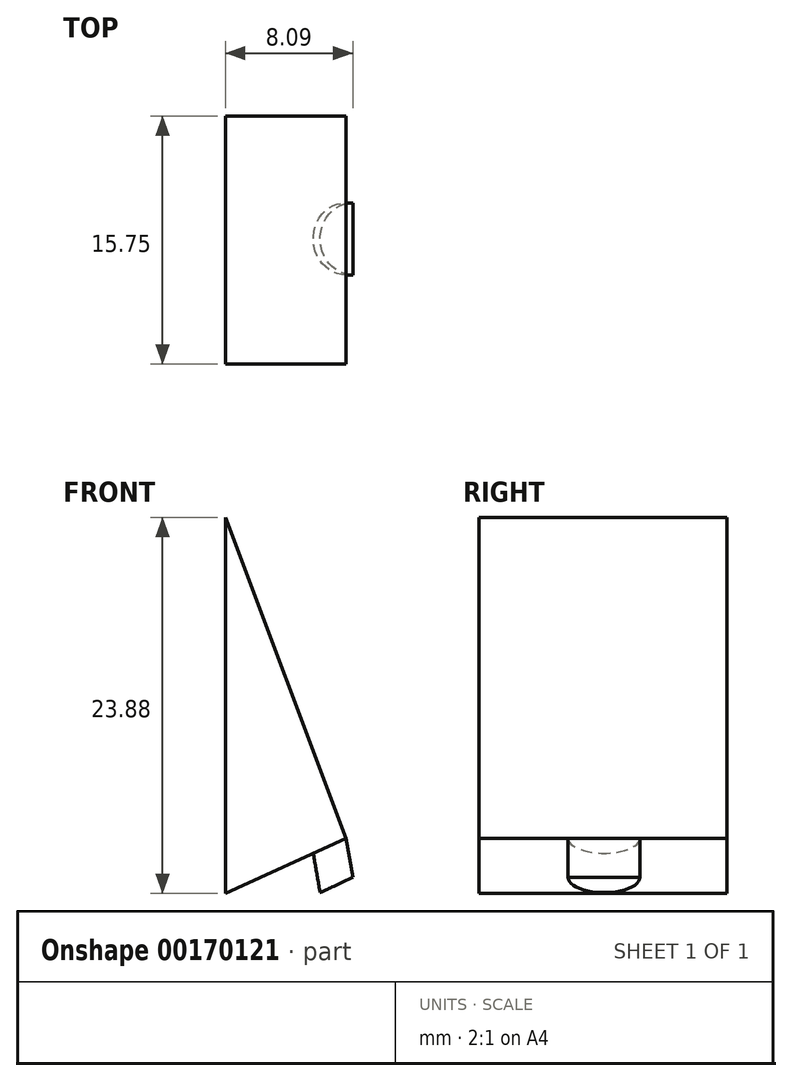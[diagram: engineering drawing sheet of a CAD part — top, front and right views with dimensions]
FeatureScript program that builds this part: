
annotation { "Feature Type Name" : "Feature", "Feature Type Description" : "" }
export const myFeature = defineFeature(function(context is Context, id is Id, definition is map)
    precondition{}
    {
        {
            var Q0;
            Q0=qCreatedBy(makeId("Front.planeOp"),FACE);
            var sketch = newSketch(context, id + "F0", { "sketchPlane" : qUnion([Q0])});
            skLineSegment(sketch, "E0", {"start": v(0, 0) * mm, "end": v(0, 23.88) * mm});
            skLineSegment(sketch, "E1", {"start": v(0, 23.88) * mm, "end": v(7.65, 3.51) * mm});
            skLineSegment(sketch, "E2", {"start": v(7.65, 3.51) * mm, "end": v(0, 0) * mm});
            skSolve(sketch);
        }
        {
            var Q0;
            Q0=makeQuery(id+"F0.imprint","IMPRINT",FACE,{"disambiguationData":[TD([[makeQuery(id+"F0.imprint","IMPRINT",EDGE,{"derivedFrom":sQuery(id+"F0.wireOp",EDGE,"E0")}),-1.0]])]});
            extrude(context, id + "F1", {"entities" : qUnion([Q0]), "depth" : 15.75 * mm});
        }
        {
            var Q0;
            Q0=makeQuery(id+"F1.opExtrude","CAP_FACE",FACE,{"disambiguationData":[OSD([sQuery(id+"F0.wireOp",EDGE,"E0"),sQuery(id+"F0.wireOp",EDGE,"E1"),sQuery(id+"F0.wireOp",EDGE,"E2")])],"isStart":false});
            cPlane(context, id + "F2", {"entities" : qUnion([Q0]), "cplaneType" : CPlaneType.OFFSET, "offset" : 7.87 * mm, "oppositeDirection" : true, "width" : 152.4 * mm, "height" : 152.4 * mm});
        }
        {
            var Q0;
            Q0=makeQuery(id+"F1.opExtrude","SWEPT_FACE",FACE,{"disambiguationData":[OSD([sQuery(id+"F0.wireOp",EDGE,"E2")])]});
            var sketch = newSketch(context, id + "F3", { "sketchPlane" : qUnion([Q0])});
            skArc(sketch, "E3", {"start": v(8.42, 10.08) * mm, "mid": v(6.14, 7.8) * mm, "end": v(8.42, 5.51) * mm});
            skSolve(sketch);
        }
        {
            var Q0;
            Q0=qCreatedBy(id+"F2.planeOp",FACE);
            var sketch = newSketch(context, id + "F4", { "sketchPlane" : qUnion([Q0])});
            skLineSegment(sketch, "E4", {"start": v(7.82, 3.35) * mm, "end": v(8.26, 0.85) * mm});
            skSolve(sketch);
        }
        {
            var Q0;
            {var subQ0=sQuery(id+"F3.wireOp",EDGE,"E3");Q0=makeQuery(id+"F3.imprint","IMPRINT",FACE,{"disambiguationData":[TD([[makeQuery(id+"F3.imprint","IMPRINT",EDGE,{"derivedFrom":subQ0}),1.0]])]});}
            var Q1;
            Q1=sQuery(id+"F4.wireOp",EDGE,"E4");
            var Q2;
            Q2=sQuery(id+"F4.wireOp",EDGE,"tmTE60SX-19qu-gUP0-lkM0-cfvha6vOpwyd");
            sweep(context, id + "F5", {"operationType" : NewBodyOperationType.ADD, "profiles" : qUnion([Q0]), "path" : qUnion([Q1, Q2])});
        }
    });
